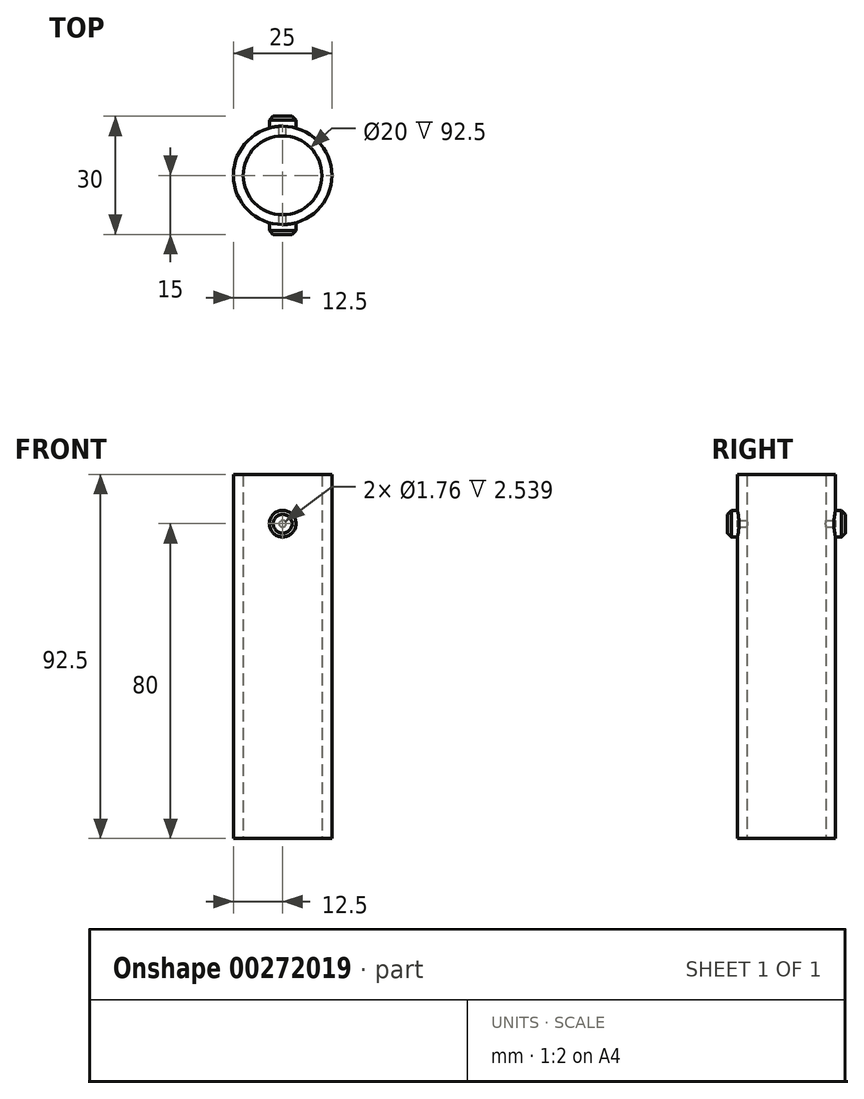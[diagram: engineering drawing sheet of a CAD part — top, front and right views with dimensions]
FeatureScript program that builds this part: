
annotation { "Feature Type Name" : "Feature", "Feature Type Description" : "" }
export const myFeature = defineFeature(function(context is Context, id is Id, definition is map)
    precondition{}
    {
        {
            var Q0;
            Q0=qCreatedBy(makeId("Front.planeOp"),FACE);
            var sketch = newSketch(context, id + "F0", { "sketchPlane" : qUnion([Q0])});
            skLineSegment(sketch, "E0", {"start": v(0, 0) * mm, "end": v(0, 80) * mm});
            skCircle(sketch, "E1", {"center": v(0, 80) * mm, "radius": 3.38 * mm});
            skSolve(sketch);
        }
        {
            var Q0;
            Q0 = qSketchRegion(id + "F0", true);
            extrude(context, id + "F1", {"entities" : qUnion([Q0]), "endBound" : BoundingType.SYMMETRIC, "depth" : 30 * mm});
        }
        {
            var Q0;
            Q0=qCreatedBy(makeId("Top.planeOp"),FACE);
            var sketch = newSketch(context, id + "F2", { "sketchPlane" : qUnion([Q0])});
            skCircle(sketch, "E2", {"center": v(0, 0) * mm, "radius": 12.5 * mm});
            skSolve(sketch);
        }
        {
            var Q0;
            Q0 = qSketchRegion(id + "F2", true);
            extrude(context, id + "F3", {"entities" : qUnion([Q0]), "operationType" : NewBodyOperationType.ADD, "depth" : 92.5 * mm});
        }
        {
            var Q0;
            Q0=makeQuery(id+"F3.opExtrude","CAP_FACE",FACE,{"disambiguationData":[OSD([sQuery(id+"F2.wireOp",EDGE,"E2")])],"isStart":false});
            var Q1;
            Q1=makeQuery(id+"F3.opExtrude","CAP_FACE",FACE,{"disambiguationData":[OSD([sQuery(id+"F2.wireOp",EDGE,"E2")])],"isStart":true});
            shell(context, id + "F4", {"entities" : qUnion([Q0, Q1]), "thickness" : 2.5 * mm});
        }
        {
            var Q0;
            Q0=makeQuery(id+"F1.opExtrude","CAP_EDGE",EDGE,{"disambiguationData":[OSD([sQuery(id+"F0.wireOp",EDGE,"E1")])],"isStart":false});
            chamfer(context, id + "F5", {"entities" : qUnion([Q0]), "width" : 1 * mm, "tangentPropagation" : true});
        }
        {
            var Q0;
            Q0=makeQuery(id+"F1.opExtrude","CAP_EDGE",EDGE,{"disambiguationData":[OSD([sQuery(id+"F0.wireOp",EDGE,"E1")])],"isStart":true});
            chamfer(context, id + "F6", {"entities" : qUnion([Q0]), "width" : 1 * mm, "tangentPropagation" : true});
        }
    });
